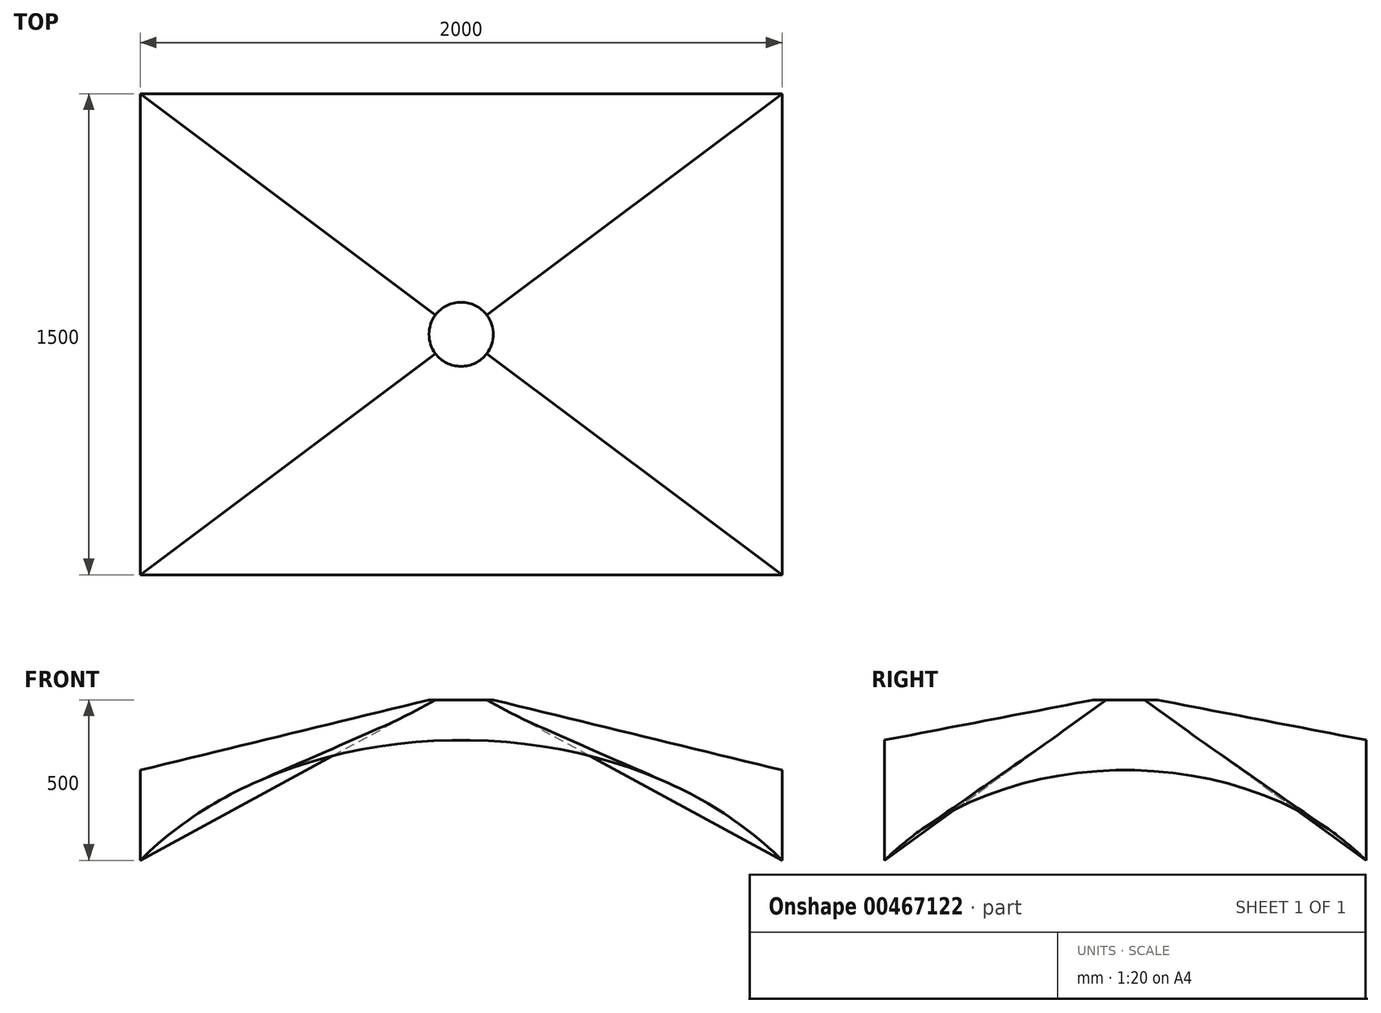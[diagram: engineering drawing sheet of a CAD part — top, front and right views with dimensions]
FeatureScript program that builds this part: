
annotation { "Feature Type Name" : "Feature", "Feature Type Description" : "" }
export const myFeature = defineFeature(function(context is Context, id is Id, definition is map)
    precondition{}
    {
        {
            assignVariable(context, id + "F0", {"name" : "Height", "anyValue" : 1000});
        }
        {
            var Q0;
            Q0=qCreatedBy(makeId("Top.planeOp"),FACE);
            var sketch = newSketch(context, id + "F1", { "sketchPlane" : qUnion([Q0])});
            skLineSegment(sketch, "E0.bottom", {"start": v(-1000, 750) * mm, "end": v(1000, 750) * mm, "construction": true});
            skLineSegment(sketch, "E0.top", {"start": v(-1000, -750) * mm, "end": v(1000, -750) * mm, "construction": true});
            skLineSegment(sketch, "E0.left", {"start": v(-1000, 750) * mm, "end": v(-1000, -750) * mm, "construction": true});
            skLineSegment(sketch, "E0.right", {"start": v(1000, 750) * mm, "end": v(1000, -750) * mm, "construction": true});
            skPoint(sketch, "E0.middle", {"position": v(0, 0) * mm});
            skSolve(sketch);
        }
        {
            var Q0;
            Q0=qCreatedBy(makeId("Front.planeOp"),FACE);
            var Q1;
            Q1=sQuery(id+"F1.wireOp",EDGE,"E0.top");
            cPlane(context, id + "F2", {"entities" : qUnion([Q0, Q1]), "cplaneType" : CPlaneType.LINE_ANGLE, "offset" : 25 * mm, "angle" : 0 * degree, "width" : 150 * mm, "height" : 150 * mm});
        }
        {
            var Q0;
            Q0=qCreatedBy(makeId("Front.planeOp"),FACE);
            var Q1;
            Q1=sQuery(id+"F1.wireOp",EDGE,"E0.bottom");
            cPlane(context, id + "F3", {"entities" : qUnion([Q0, Q1]), "cplaneType" : CPlaneType.LINE_ANGLE, "offset" : 25 * mm, "angle" : 0 * degree, "width" : 150 * mm, "height" : 150 * mm});
        }
        {
            var Q0;
            Q0=sQuery(id+"F1.wireOp",EDGE,"E0.right");
            var Q1;
            Q1=qCreatedBy(makeId("Right.planeOp"),FACE);
            cPlane(context, id + "F4", {"entities" : qUnion([Q0, Q1]), "cplaneType" : CPlaneType.LINE_ANGLE, "offset" : 25 * mm, "angle" : 0 * degree, "width" : 150 * mm, "height" : 150 * mm});
        }
        {
            var Q0;
            Q0=sQuery(id+"F1.wireOp",EDGE,"E0.left");
            var Q1;
            Q1=qCreatedBy(makeId("Right.planeOp"),FACE);
            cPlane(context, id + "F5", {"entities" : qUnion([Q0, Q1]), "cplaneType" : CPlaneType.LINE_ANGLE, "offset" : 25 * mm, "angle" : 0 * degree, "width" : 150 * mm, "height" : 150 * mm});
        }
        {
            var Q0;
            Q0=qCreatedBy(id+"F2.planeOp",FACE);
            var sketch = newSketch(context, id + "F6", { "sketchPlane" : qUnion([Q0])});
            skPoint(sketch, "E1.0", {"position": v(1000, 0) * mm});
            skPoint(sketch, "E2.0", {"position": v(-1000, 0) * mm});
            skPoint(sketch, "E3", {"position": v(1000, 500) * mm});
            skPoint(sketch, "E4", {"position": v(-1000, 500) * mm});
            skFitSpline(sketch, "E5", {"points": [v(1000, 500) * mm, v(-1000, 500) * mm], "startDerivative": vector(-1500, 1500) * mm, "endDerivative": vector(-1500, -1500) * mm});
            skLineSegment(sketch, "E6", {"start": v(1000, 500) * mm, "end": v(500, 1000) * mm, "construction": true});
            skLineSegment(sketch, "E7", {"start": v(-500, 1000) * mm, "end": v(-1000, 500) * mm, "construction": true});
            skLineSegment(sketch, "E8", {"start": v(-1000, 500) * mm, "end": v(-839.98, 500) * mm, "construction": true});
            skLineSegment(sketch, "E9", {"start": v(1000, 500) * mm, "end": v(775.13, 500) * mm, "construction": true});
            skSolve(sketch);
        }
        {
            var Q0;
            Q0=qCreatedBy(id+"F3.planeOp",FACE);
            var sketch = newSketch(context, id + "F7", { "sketchPlane" : qUnion([Q0])});
            skPoint(sketch, "E10.0", {"position": v(-1000, 0) * mm});
            skPoint(sketch, "E11.0", {"position": v(1000, 0) * mm});
            skPoint(sketch, "E12", {"position": v(-1000, 500) * mm});
            skPoint(sketch, "E13", {"position": v(1000, 500) * mm});
            skFitSpline(sketch, "E14", {"points": [v(-1000, 500) * mm, v(1000, 500) * mm], "startDerivative": vector(1500, 1500) * mm, "endDerivative": vector(1500, -1500) * mm});
            skLineSegment(sketch, "E15", {"start": v(-1000, 500) * mm, "end": v(-774.02, 500) * mm, "construction": true});
            skLineSegment(sketch, "E16", {"start": v(-500, 1000) * mm, "end": v(-1000, 500) * mm, "construction": true});
            skLineSegment(sketch, "E17", {"start": v(1000, 500) * mm, "end": v(812.8, 500) * mm, "construction": true});
            skLineSegment(sketch, "E18", {"start": v(1000, 500) * mm, "end": v(500, 1000) * mm, "construction": true});
            skSolve(sketch);
        }
        {
            var Q0;
            Q0=qCreatedBy(id+"F4.planeOp",FACE);
            var sketch = newSketch(context, id + "F8", { "sketchPlane" : qUnion([Q0])});
            skPoint(sketch, "E19.0", {"position": v(-750, 500) * mm});
            skPoint(sketch, "E20.0", {"position": v(750, 500) * mm});
            skFitSpline(sketch, "E21", {"points": [v(-750, 500) * mm, v(750, 500) * mm], "startDerivative": vector(1125, 1125) * mm, "endDerivative": vector(1125, -1125) * mm});
            skLineSegment(sketch, "E22", {"start": v(-375, 875) * mm, "end": v(-750, 500) * mm, "construction": true});
            skLineSegment(sketch, "E23", {"start": v(-520.22, 500) * mm, "end": v(-750, 500) * mm, "construction": true});
            skLineSegment(sketch, "E24", {"start": v(375, 875) * mm, "end": v(750, 500) * mm, "construction": true});
            skLineSegment(sketch, "E25", {"start": v(630.57, 500) * mm, "end": v(750, 500) * mm, "construction": true});
            skSolve(sketch);
        }
        {
            var Q0;
            Q0=qCreatedBy(id+"F5.planeOp",FACE);
            var sketch = newSketch(context, id + "F9", { "sketchPlane" : qUnion([Q0])});
            skPoint(sketch, "E26.0", {"position": v(-750, 500) * mm});
            skPoint(sketch, "E27.0", {"position": v(750, 500) * mm});
            skFitSpline(sketch, "E28", {"points": [v(-750, 500) * mm, v(750, 500) * mm], "startDerivative": vector(1125, 1125) * mm, "endDerivative": vector(1125, -1125) * mm});
            skLineSegment(sketch, "E29", {"start": v(-375, 875) * mm, "end": v(-750, 500) * mm, "construction": true});
            skLineSegment(sketch, "E30", {"start": v(375, 875) * mm, "end": v(750, 500) * mm, "construction": true});
            skSolve(sketch);
        }
        {
            var Q0;
            Q0=qCreatedBy(makeId("Top.planeOp"),FACE);
            cPlane(context, id + "F10", {"entities" : qUnion([Q0]), "cplaneType" : CPlaneType.OFFSET, "offset" : (getVariable(context, 'Height')) * mm, "width" : 150 * mm, "height" : 150 * mm});
        }
        {
            var Q0;
            Q0=qCreatedBy(id+"F10.planeOp",FACE);
            var sketch = newSketch(context, id + "F11", { "sketchPlane" : qUnion([Q0])});
            skPoint(sketch, "E31.0", {"position": v(-1000, 750) * mm});
            skPoint(sketch, "E32.0", {"position": v(-1000, -750) * mm});
            skPoint(sketch, "E33.0", {"position": v(1000, -750) * mm});
            skPoint(sketch, "E34.0", {"position": v(1000, 750) * mm});
            skLineSegment(sketch, "E35", {"start": v(0, 0) * mm, "end": v(-1000, 750) * mm});
            skLineSegment(sketch, "E36", {"start": v(0, 0) * mm, "end": v(1000, 750) * mm});
            skLineSegment(sketch, "E37", {"start": v(0, 0) * mm, "end": v(1000, -750) * mm});
            skLineSegment(sketch, "E38", {"start": v(0, 0) * mm, "end": v(-1000, -750) * mm});
            skArc(sketch, "E39", {"start": v(80, 60) * mm, "mid": v(0, 100) * mm, "end": v(-80, 60) * mm});
            skArc(sketch, "E40", {"start": v(-80, 60) * mm, "mid": v(-100, 0) * mm, "end": v(-80, -60) * mm});
            skArc(sketch, "E41.1.0", {"start": v(-80, -60) * mm, "mid": v(0, -100) * mm, "end": v(80, -60) * mm});
            skArc(sketch, "E42.1.0", {"start": v(80, -60) * mm, "mid": v(100, 0) * mm, "end": v(80, 60) * mm});
            skSolve(sketch);
        }
        {
            var Q0;
            Q0=sQuery(id+"F6.wireOp",EDGE,"E5");
            var Q1;
            Q1=sQuery(id+"F11.wireOp",EDGE,"E41.1.0");
            loft(context, id + "F12", {"bodyType" : ToolBodyType.SURFACE, "wireProfilesArray" : [{ "wireProfileEntities" : qUnion([Q0]) }, { "wireProfileEntities" : qUnion([Q1]) }]});
        }
        {
            var Q0;
            Q0=sQuery(id+"F8.wireOp",EDGE,"E21");
            var Q1;
            Q1=sQuery(id+"F11.wireOp",EDGE,"E42.1.0");
            loft(context, id + "F13", {"bodyType" : ToolBodyType.SURFACE, "wireProfilesArray" : [{ "wireProfileEntities" : qUnion([Q0]) }, { "wireProfileEntities" : qUnion([Q1]) }]});
        }
        {
            var Q0;
            Q0=sQuery(id+"F7.wireOp",EDGE,"E14");
            var Q1;
            Q1=sQuery(id+"F11.wireOp",EDGE,"E39");
            loft(context, id + "F14", {"bodyType" : ToolBodyType.SURFACE, "wireProfilesArray" : [{ "wireProfileEntities" : qUnion([Q0]) }, { "wireProfileEntities" : qUnion([Q1]) }]});
        }
        {
            var Q0;
            Q0=sQuery(id+"F9.wireOp",EDGE,"E28");
            var Q1;
            Q1=sQuery(id+"F11.wireOp",EDGE,"E40");
            loft(context, id + "F15", {"bodyType" : ToolBodyType.SURFACE, "wireProfilesArray" : [{ "wireProfileEntities" : qUnion([Q0]) }, { "wireProfileEntities" : qUnion([Q1]) }]});
        }
    });
